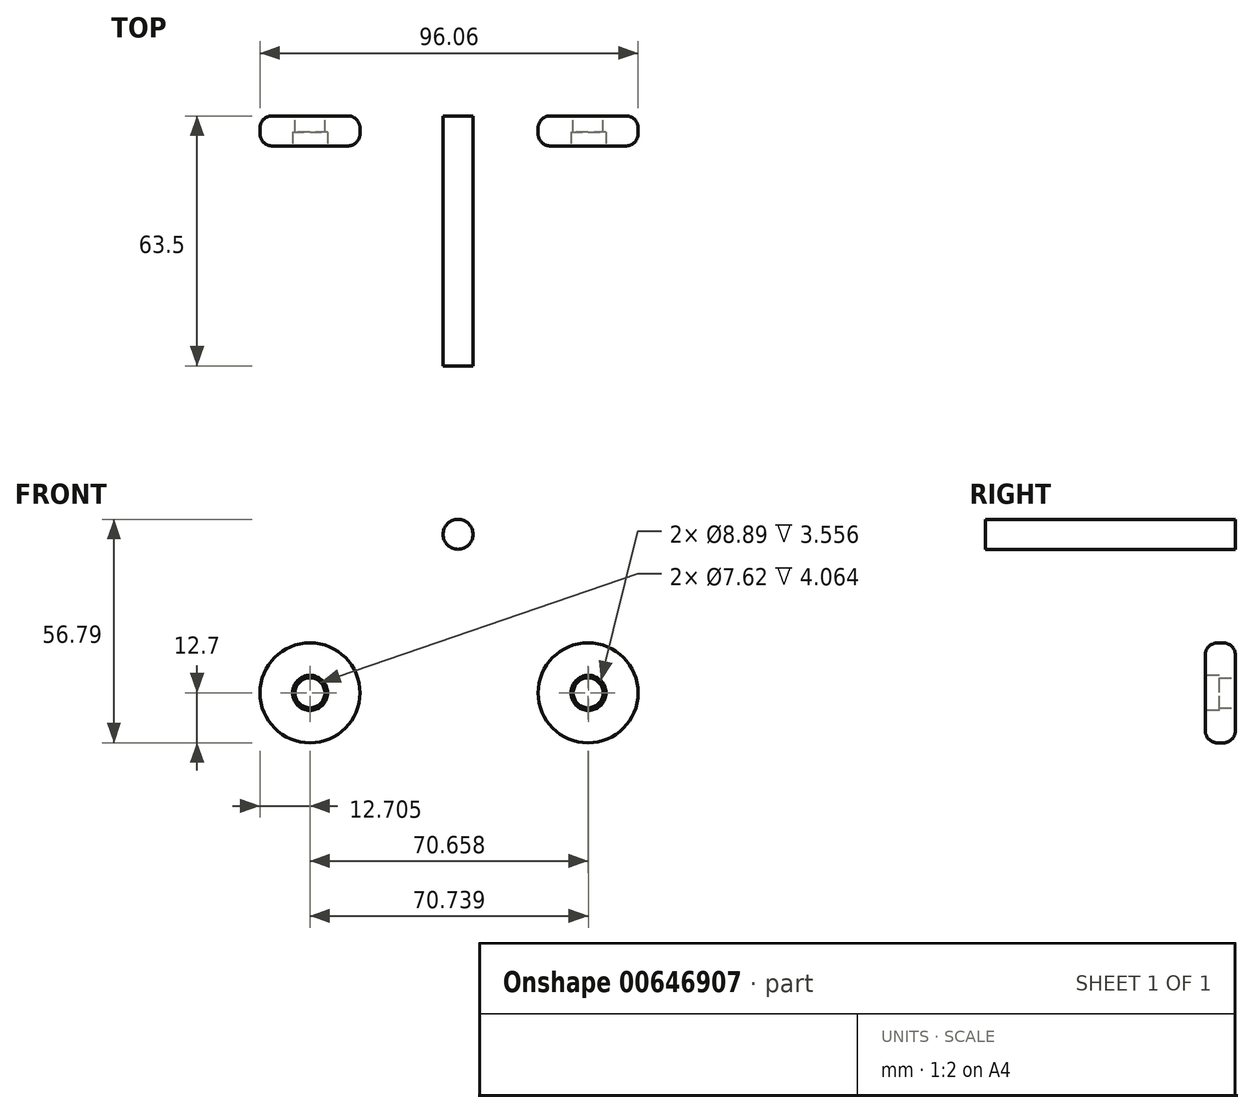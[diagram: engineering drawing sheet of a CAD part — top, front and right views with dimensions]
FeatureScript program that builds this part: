
annotation { "Feature Type Name" : "Feature", "Feature Type Description" : "" }
export const myFeature = defineFeature(function(context is Context, id is Id, definition is map)
    precondition{}
    {
        {
            var Q0;
            Q0=qCreatedBy(makeId("Front.planeOp"),FACE);
            var sketch = newSketch(context, id + "F0", { "sketchPlane" : qUnion([Q0])});
            skCircle(sketch, "E0", {"center": v(-37.62, 0) * mm, "radius": 12.7 * mm});
            skCircle(sketch, "E1", {"center": v(33.04, 0) * mm, "radius": 12.7 * mm});
            skSolve(sketch);
        }
        {
            var Q0;
            Q0 = qSketchRegion(id + "F0", true);
            extrude(context, id + "F1", {"entities" : qUnion([Q0]), "depth" : 7.62 * mm, "offsetDistance" : 25.4 * mm});
        }
        {
            var Q0;
            Q0=makeQuery(id+"F1.opExtrude","CAP_EDGE",EDGE,{"disambiguationData":[OSD([sQuery(id+"F0.wireOp",EDGE,"E1")])],"isStart":false});
            var Q1;
            Q1=makeQuery(id+"F1.opExtrude","CAP_EDGE",EDGE,{"disambiguationData":[OSD([sQuery(id+"F0.wireOp",EDGE,"E1")])],"isStart":true});
            var Q2;
            Q2=makeQuery(id+"F1.opExtrude","CAP_EDGE",EDGE,{"disambiguationData":[OSD([sQuery(id+"F0.wireOp",EDGE,"E0")])],"isStart":true});
            var Q3;
            Q3=makeQuery(id+"F1.opExtrude","CAP_EDGE",EDGE,{"disambiguationData":[OSD([sQuery(id+"F0.wireOp",EDGE,"E0")])],"isStart":false});
            fillet(context, id + "F2", {"entities" : qUnion([Q0, Q1, Q2, Q3]), "radius" : 3.07 * mm, "tangentPropagation" : true, "allowEdgeOverflow" : false});
        }
        {
            var Q0;
            Q0=makeQuery(id+"F1.opExtrude","CAP_FACE",FACE,{"disambiguationData":[OSD([sQuery(id+"F0.wireOp",EDGE,"E0")])],"isStart":false});
            var sketch = newSketch(context, id + "F3", { "sketchPlane" : qUnion([Q0])});
            skCircle(sketch, "E2", {"center": v(-37.62, 0) * mm, "radius": 4.45 * mm});
            skCircle(sketch, "E3", {"center": v(33.12, 0) * mm, "radius": 4.45 * mm});
            skSolve(sketch);
        }
        {
            var Q0;
            Q0 = qSketchRegion(id + "F3", true);
            extrude(context, id + "F4", {"entities" : qUnion([Q0]), "operationType" : NewBodyOperationType.REMOVE, "oppositeDirection" : true, "depth" : 3.56 * mm, "offsetDistance" : 25.4 * mm});
        }
        {
            var Q0;
            Q0=makeQuery(id+"F1.opExtrude","CAP_FACE",FACE,{"disambiguationData":[OSD([sQuery(id+"F0.wireOp",EDGE,"E0")])],"isStart":true});
            var sketch = newSketch(context, id + "F5", { "sketchPlane" : qUnion([Q0])});
            skCircle(sketch, "E4", {"center": v(37.62, 0) * mm, "radius": 3.81 * mm});
            skSolve(sketch);
        }
        {
            var Q0;
            Q0 = qSketchRegion(id + "F5", true);
            extrude(context, id + "F6", {"entities" : qUnion([Q0]), "operationType" : NewBodyOperationType.REMOVE, "oppositeDirection" : true, "depth" : 5.08 * mm, "offsetDistance" : 25.4 * mm});
        }
        {
            var Q0;
            Q0=makeQuery(id+"F1.opExtrude","CAP_FACE",FACE,{"disambiguationData":[OSD([sQuery(id+"F0.wireOp",EDGE,"E1")])],"isStart":true});
            var sketch = newSketch(context, id + "F7", { "sketchPlane" : qUnion([Q0])});
            skCircle(sketch, "E5", {"center": v(-33.04, 0) * mm, "radius": 3.81 * mm});
            skSolve(sketch);
        }
        {
            var Q0;
            Q0 = qSketchRegion(id + "F7", true);
            extrude(context, id + "F8", {"entities" : qUnion([Q0]), "operationType" : NewBodyOperationType.REMOVE, "oppositeDirection" : true, "depth" : 5.08 * mm, "offsetDistance" : 25.4 * mm});
        }
        {
            var Q0;
            Q0=qCreatedBy(makeId("Front.planeOp"),FACE);
            var sketch = newSketch(context, id + "F9", { "sketchPlane" : qUnion([Q0])});
            skCircle(sketch, "E6", {"center": v(0, 40.28) * mm, "radius": 3.81 * mm});
            skSolve(sketch);
        }
        {
            var Q0;
            Q0 = qSketchRegion(id + "F9", true);
            extrude(context, id + "F10", {"entities" : qUnion([Q0]), "depth" : 63.5 * mm, "offsetDistance" : 25.4 * mm});
        }
    });
